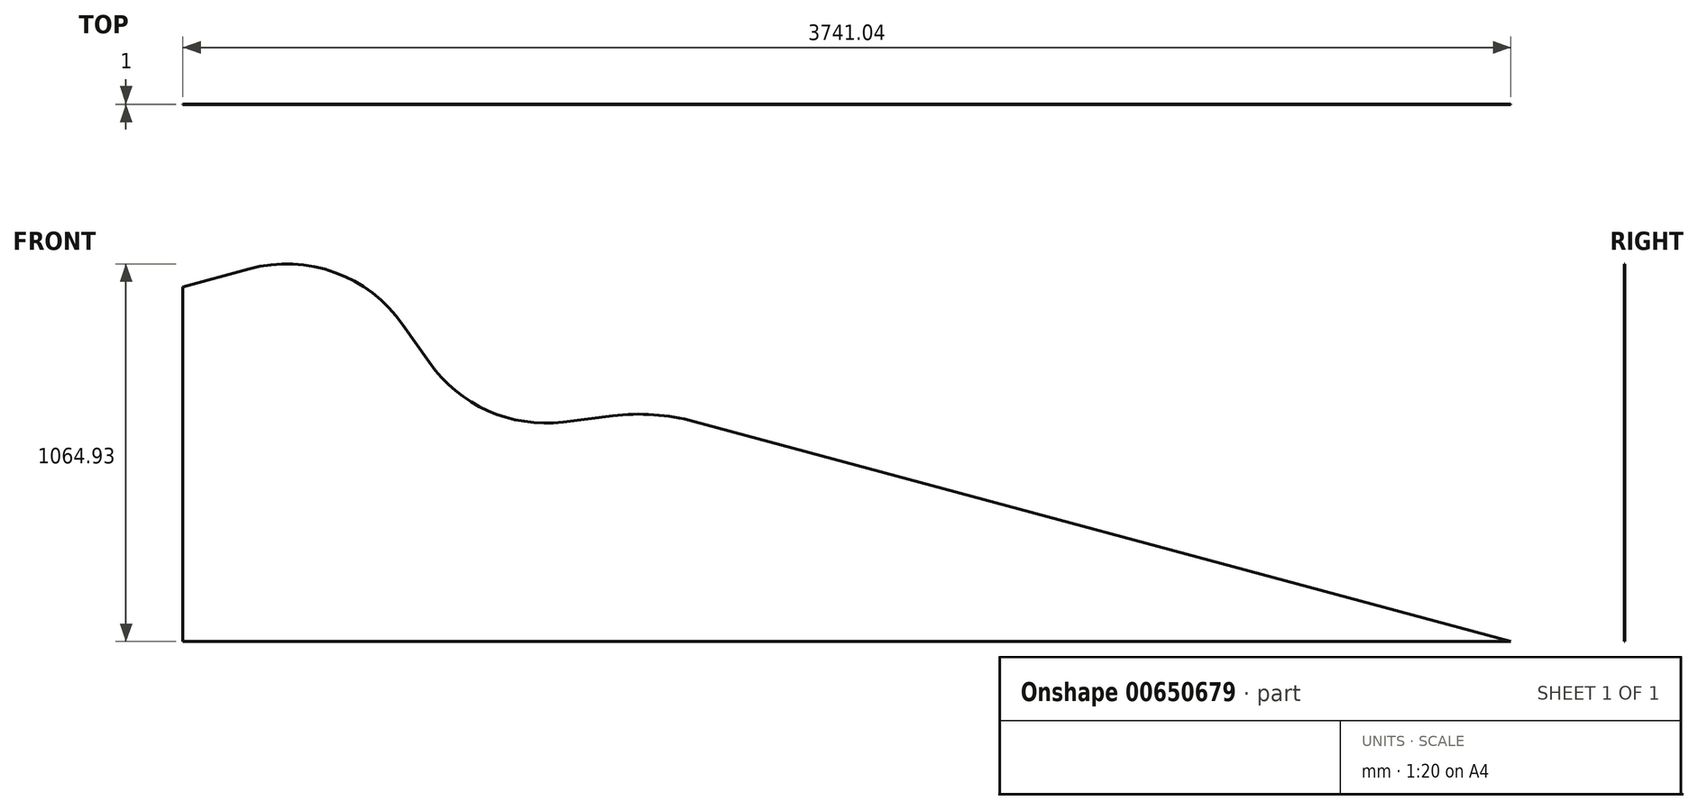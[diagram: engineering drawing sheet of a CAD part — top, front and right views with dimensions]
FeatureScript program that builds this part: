
annotation { "Feature Type Name" : "Feature", "Feature Type Description" : "" }
export const myFeature = defineFeature(function(context is Context, id is Id, definition is map)
    precondition{}
    {
        {
            var Q0;
            Q0=qCreatedBy(makeId("Front.planeOp"),FACE);
            var sketch = newSketch(context, id + "F0", { "sketchPlane" : qUnion([Q0])});
            skLineSegment(sketch, "E0", {"start": v(-1139.41, -389.94) * mm, "end": v(-1139.41, 610.06) * mm});
            skLineSegment(sketch, "E1", {"start": v(-1139.41, 610.06) * mm, "end": v(-953.03, 660.9) * mm});
            skLineSegment(sketch, "E2", {"start": v(-519.66, 503.77) * mm, "end": v(-445.64, 397.6) * mm});
            skLineSegment(sketch, "E3", {"start": v(-68.32, 229.43) * mm, "end": v(71.2, 246.72) * mm});
            skLineSegment(sketch, "E4", {"start": v(301.28, 230.57) * mm, "end": v(2601.63, -389.94) * mm});
            skLineSegment(sketch, "E5", {"start": v(2601.63, -389.94) * mm, "end": v(-1139.41, -389.94) * mm});
            skPoint(sketch, "E6.visualSharp", {"position": v(-680.96, 735.1) * mm});
            skArc(sketch, "E6.filletArc", {"start": v(-519.66, 503.77) * mm, "mid": v(-711.43, 651.04) * mm, "end": v(-953.03, 660.9) * mm});
            skPoint(sketch, "E7.visualSharp", {"position": v(-307.69, 199.75) * mm});
            skArc(sketch, "E7.filletArc", {"start": v(-445.64, 397.6) * mm, "mid": v(-280.37, 261.04) * mm, "end": v(-68.32, 229.43) * mm});
            skPoint(sketch, "E8.visualSharp", {"position": v(187.82, 261.18) * mm});
            skArc(sketch, "E8.filletArc", {"start": v(301.28, 230.57) * mm, "mid": v(187.02, 249.8) * mm, "end": v(71.2, 246.72) * mm});
            skSolve(sketch);
        }
        {
            var Q0;
            Q0 = qSketchRegion(id + "F0", true);
            extrude(context, id + "F1", {"entities" : qUnion([Q0]), "depth" : 1 * mm, "offsetDistance" : 25 * mm});
        }
    });
